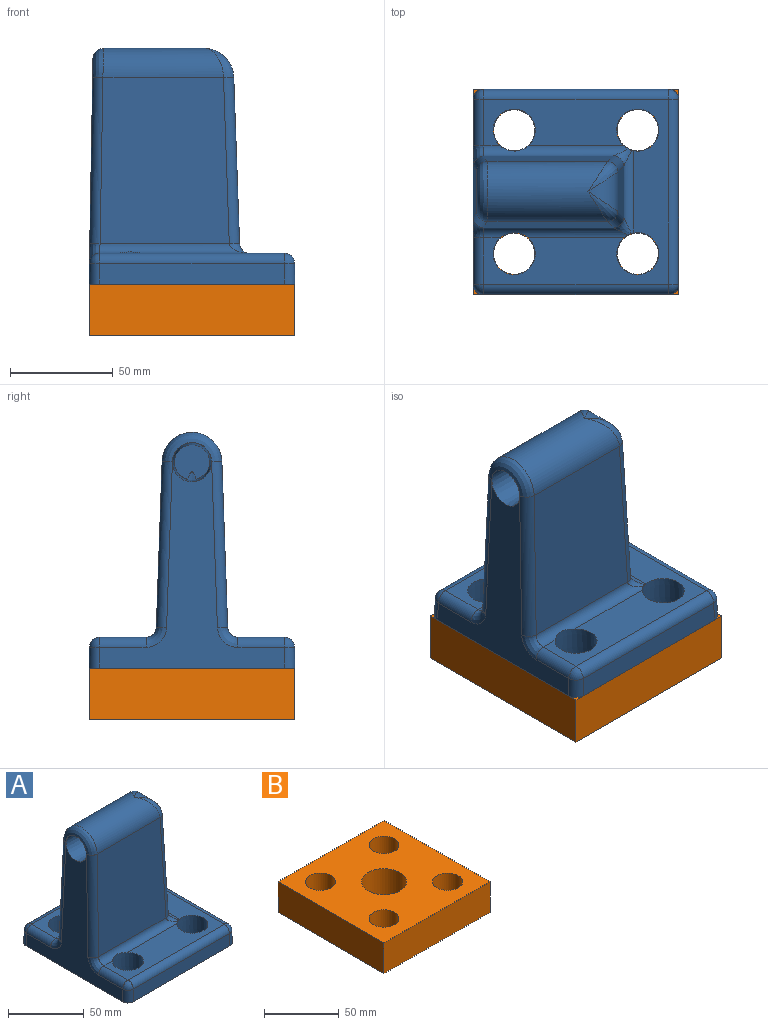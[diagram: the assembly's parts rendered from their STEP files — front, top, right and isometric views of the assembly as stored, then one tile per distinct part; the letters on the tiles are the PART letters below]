
ASSEMBLY  parts=2 mates=1
PART A: 53 faces, bbox 100.9x100.9x115.4 mm
  f0: plane 36.02x36.02mm, normal (0,0,-1), area 311.1mm2, adj f6,f29
  f1: plane 90x10.09mm, normal (1,0,0.02), area 906.2mm2, adj f14,f24,f49,f51
  f2: cylinder r=5mm len=89.65mm, axis (-1,0,0), area 696.3mm2, adj f11,f15,f39,f50
  f3: plane 80.68x62.76mm, normal (0,-1,0.03), area 4896.2mm2, adj f9,f16,f36,f42
  f4: plane 80.68x62.76mm, normal (0,1,0.03), area 4896.2mm2, adj f10,f16,f34,f46
  f5: cylinder r=5mm len=89.65mm, axis (-1,0,0), area 696.3mm2, adj f12,f15,f31,f52
  f6: cone r=15mm half-angle=3deg, axis (0,0,-1), area 7552.7mm2, adj f0,f7,f8,f21,f22
  f7: plane 9.03x1.19mm, normal (0,0,-1), area 6.8mm2, adj f6,f21
  f8: plane 9.03x1.19mm, normal (0,0,-1), area 6.8mm2, adj f6,f21
  f9: cylinder r=5mm len=70.14mm, axis (-1,0,0), area 483.7mm2, adj f3,f15,f19,f20,f37,f41
  f10: cylinder r=5mm len=70.14mm, axis (-1,0,0), area 483.7mm2, adj f4,f15,f17,f18,f33,f45
  f11: plane 90x10.09mm, normal (0,-1,0.02), area 906.2mm2, adj f2,f14,f40,f49
  f12: plane 90x10.09mm, normal (0,1,0.02), area 906.2mm2, adj f5,f14,f30,f51
  f13: plane 110.28x90.66mm, normal (-1,0,0.02), area 2803.8mm2, adj f14,f21,f30,f32,f33,f34,f35,f36
  f14: plane 100.07x100.07mm, normal (0,0,-1), area 6648.8mm2, adj f1,f11,f12,f13,f17,f18,f19,f20
  f15: plane 89.65x89.65mm, normal (0,0,1), area 3530.3mm2, adj f2,f5,f9,f10,f17,f18,f19,f20
  f16: cylinder r=14.53mm len=58.54mm, axis (-1,0,0), area 2450.1mm2, adj f3,f4,f35,f43,f44,f47,f48
  f17: cone r=11mm half-angle=3deg, axis (0,0,-1), area 1001.7mm2, adj f10,f14,f15,f25,f45
  f18: cone r=11mm half-angle=3deg, axis (0,0,-1), area 1001.1mm2, adj f10,f14,f15
  f19: cone r=11mm half-angle=3deg, axis (0,0,-1), area 1001.1mm2, adj f9,f14,f15
  f20: cone r=11mm half-angle=3deg, axis (0,0,-1), area 1001.7mm2, adj f9,f14,f15,f25,f41
  f21: cone r=9.53mm half-angle=1deg, axis (-1,0,0), area 2891.2mm2, adj f6,f7,f8,f13,f22
  f22: plane 17.84x17.61mm, normal (-1,0,0), area 215.6mm2, adj f6,f21
  f23: plane 80.71x24.67mm, normal (1,0,0.03), area 1764.9mm2, adj f25,f26,f42,f43,f46,f47
  f24: cylinder r=5mm len=89.65mm, axis (0,-1,0), area 696.3mm2, adj f1,f15,f50,f52
  f25: cylinder r=5mm len=40.46mm, axis (0,-1,0), area 244mm2, adj f15,f17,f20,f23,f41,f45
  f26: cylinder r=14.5mm len=19.04mm, axis (0,-1,0), area 212mm2, adj f23,f44,f48
  f27: plane 47.92x47.92mm, normal (0,0,-1), area 780.6mm2, adj f28,f29
  f28: cone r=24mm half-angle=1deg, axis (0,0,-1), area 361.5mm2, adj f14,f27
  f29: cone r=18mm half-angle=1deg, axis (0,0,1), area 271.7mm2, adj f0,f27
  f30: cylinder r=5mm len=10.12mm, axis (-0.02,0.02,-1), area 79.2mm2, adj f12,f13,f14,f31
  f31: sphere r=5mm, area 21.8mm2, adj f5,f30,f32
  f32: cylinder r=5mm len=22.49mm, axis (0,1,0), area 174.7mm2, adj f13,f15,f31,f33
  f33: bspline ~10.44x10mm, area 81.8mm2, adj f10,f13,f32,f34
  f34: cylinder r=5mm len=80.79mm, axis (0.02,-0.03,1), area 633.9mm2, adj f4,f13,f33,f35
  f35: bspline ~29.06x15.16mm, area 304.1mm2, adj f13,f16,f34,f36
  f36: cylinder r=5mm len=80.79mm, axis (-0.02,-0.03,-1), area 633.9mm2, adj f3,f13,f35,f37
  f37: bspline ~10.44x10mm, area 81.8mm2, adj f9,f13,f36,f38
  f38: cylinder r=5mm len=22.49mm, axis (0,-1,0), area 174.7mm2, adj f13,f15,f37,f39
  f39: sphere r=5mm, area 24.2mm2, adj f2,f38,f40
  f40: cylinder r=5mm len=10.12mm, axis (-0.02,-0.02,-1), area 79.2mm2, adj f11,f13,f14,f39
  f41: bspline ~8.94x8.94mm, area 43.9mm2, adj f9,f20,f25,f42
  f42: cylinder r=5mm len=80.75mm, axis (-0.03,0.03,1), area 634mm2, adj f3,f23,f41,f43
  f43: bspline ~5x5mm, area 0.3mm2, adj f16,f23,f42,f44
  f44: bspline ~17.19x14.55mm, area 80mm2, adj f16,f26,f43
  f45: bspline ~8.94x8.94mm, area 43.9mm2, adj f10,f17,f25,f46
  f46: cylinder r=5mm len=80.75mm, axis (0.03,0.03,-1), area 634mm2, adj f4,f23,f45,f47
  f47: bspline ~5x5mm, area 0.3mm2, adj f16,f23,f46,f48
  f48: bspline ~17.19x14.55mm, area 80mm2, adj f16,f26,f47
  f49: cylinder r=5mm len=10.12mm, axis (0.02,-0.02,-1), area 79.2mm2, adj f1,f11,f14,f50
  f50: sphere r=5mm, area 38.4mm2, adj f2,f24,f49
  f51: cylinder r=5mm len=10.12mm, axis (0.02,0.02,-1), area 79.2mm2, adj f1,f12,f14,f52
  f52: sphere r=5mm, area 24.6mm2, adj f5,f24,f51
PART B: 11 faces, bbox 100x100x25 mm
  f0: plane 100x25mm, normal (0,-1,0), area 2500mm2, adj f1,f8,f9,f10
  f1: plane 100x25mm, normal (1,0,0), area 2500mm2, adj f0,f2,f9,f10
  f2: plane 100x25mm, normal (0,1,0), area 2500mm2, adj f1,f8,f9,f10
  f3: cylinder r=15mm len=30mm, axis (0,0,-1), area 2356.2mm2, adj f9,f10
  f4: cylinder r=10mm len=25mm, axis (0,0,-1), area 1570.8mm2, adj f9,f10
  f5: cylinder r=10mm len=25mm, axis (0,0,-1), area 1570.8mm2, adj f9,f10
  f6: cylinder r=10mm len=25mm, axis (0,0,-1), area 1570.8mm2, adj f9,f10
  f7: cylinder r=10mm len=25mm, axis (0,0,-1), area 1570.8mm2, adj f9,f10
  f8: plane 100x25mm, normal (-1,0,0), area 2500mm2, adj f0,f2,f9,f10
  f9: plane 100x100mm, normal (0,0,1), area 8036.5mm2, adj f0,f1,f2,f3,f4,f5,f6,f7
  f10: plane 100x100mm, normal (0,0,-1), area 8036.5mm2, adj f0,f1,f2,f3,f4,f5,f6,f7
PLACE A t=(-35.97,-19,15.15)mm
PLACE B t=(-35.97,-19,-9.85)mm fixed
MATE fastened B.f3 <-> A.f6  axis (0,0,1) through (-35.97,-19,15.15)mm
